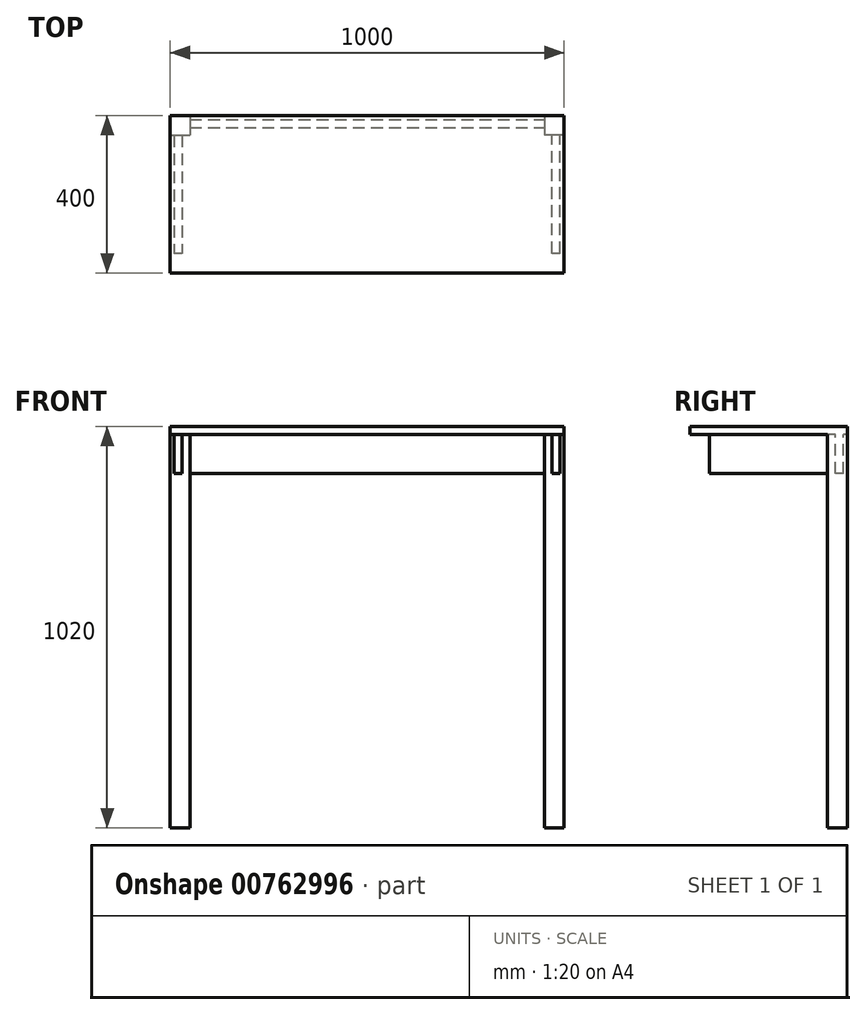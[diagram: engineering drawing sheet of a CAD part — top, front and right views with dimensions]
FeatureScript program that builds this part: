
annotation { "Feature Type Name" : "Feature", "Feature Type Description" : "" }
export const myFeature = defineFeature(function(context is Context, id is Id, definition is map)
    precondition{}
    {
        {
            var Q0;
            Q0=qCreatedBy(makeId("Top.planeOp"),FACE);
            var sketch = newSketch(context, id + "F0", { "sketchPlane" : qUnion([Q0])});
            skLineSegment(sketch, "E0.bottom", {"start": v(0, 0) * mm, "end": v(-1000, 0) * mm});
            skLineSegment(sketch, "E0.top", {"start": v(0, -400) * mm, "end": v(-1000, -400) * mm});
            skLineSegment(sketch, "E0.left", {"start": v(0, 0) * mm, "end": v(0, -400) * mm});
            skLineSegment(sketch, "E0.right", {"start": v(-1000, 0) * mm, "end": v(-1000, -400) * mm});
            skSolve(sketch);
        }
        {
            var Q0;
            Q0=makeQuery(id+"F0.imprint","IMPRINT",FACE,{"disambiguationData":[TD([[makeQuery(id+"F0.imprint","IMPRINT",EDGE,{"derivedFrom":sQuery(id+"F0.wireOp",EDGE,"E0.bottom")}),1.0]])]});
            extrude(context, id + "F1", {"entities" : qUnion([Q0]), "oppositeDirection" : true, "depth" : 20 * mm, "offsetDistance" : 25 * mm});
        }
        {
            var Q0;
            Q0=makeQuery(id+"F1.opExtrude","CAP_FACE",FACE,{"disambiguationData":[OSD([sQuery(id+"F0.wireOp",EDGE,"E0.bottom"),sQuery(id+"F0.wireOp",EDGE,"E0.top"),sQuery(id+"F0.wireOp",EDGE,"E0.left"),sQuery(id+"F0.wireOp",EDGE,"E0.right")])],"isStart":false});
            var sketch = newSketch(context, id + "F2", { "sketchPlane" : qUnion([Q0])});
            skLineSegment(sketch, "E1.bottom", {"start": v(0, 0) * mm, "end": v(-50, 0) * mm});
            skLineSegment(sketch, "E1.top", {"start": v(0, 50) * mm, "end": v(-50, 50) * mm});
            skLineSegment(sketch, "E1.left", {"start": v(0, 0) * mm, "end": v(0, 50) * mm});
            skLineSegment(sketch, "E1.right", {"start": v(-50, 0) * mm, "end": v(-50, 50) * mm});
            skLineSegment(sketch, "E2.bottom", {"start": v(-1000, 0) * mm, "end": v(-950, 0) * mm});
            skLineSegment(sketch, "E2.top", {"start": v(-1000, 50) * mm, "end": v(-950, 50) * mm});
            skLineSegment(sketch, "E2.left", {"start": v(-1000, 0) * mm, "end": v(-1000, 50) * mm});
            skLineSegment(sketch, "E2.right", {"start": v(-950, 0) * mm, "end": v(-950, 50) * mm});
            skSolve(sketch);
        }
        {
            var Q0;
            Q0 = qSketchRegion(id + "F2", true);
            extrude(context, id + "F3", {"entities" : qUnion([Q0]), "operationType" : NewBodyOperationType.ADD, "depth" : 1000 * mm, "offsetDistance" : 25 * mm});
        }
        {
            var Q0;
            Q0=makeQuery(id+"F1.opExtrude","CAP_FACE",FACE,{"disambiguationData":[OSD([sQuery(id+"F0.wireOp",EDGE,"E0.bottom"),sQuery(id+"F0.wireOp",EDGE,"E0.top"),sQuery(id+"F0.wireOp",EDGE,"E0.left"),sQuery(id+"F0.wireOp",EDGE,"E0.right")])],"isStart":false});
            var sketch = newSketch(context, id + "F4", { "sketchPlane" : qUnion([Q0])});
            skLineSegment(sketch, "E3.bottom", {"start": v(-950, 10) * mm, "end": v(-50, 10) * mm});
            skLineSegment(sketch, "E3.top", {"start": v(-950, 30) * mm, "end": v(-50, 30) * mm});
            skLineSegment(sketch, "E3.left", {"start": v(-950, 10) * mm, "end": v(-950, 30) * mm});
            skLineSegment(sketch, "E3.right", {"start": v(-50, 10) * mm, "end": v(-50, 30) * mm});
            skLineSegment(sketch, "E4.bottom", {"start": v(-10, 350) * mm, "end": v(-30, 350) * mm});
            skLineSegment(sketch, "E4.top", {"start": v(-10, 50) * mm, "end": v(-30, 50) * mm});
            skLineSegment(sketch, "E4.left", {"start": v(-10, 350) * mm, "end": v(-10, 50) * mm});
            skLineSegment(sketch, "E4.right", {"start": v(-30, 350) * mm, "end": v(-30, 50) * mm});
            skLineSegment(sketch, "E5.bottom", {"start": v(-970, 50) * mm, "end": v(-990, 50) * mm});
            skLineSegment(sketch, "E5.top", {"start": v(-970, 350) * mm, "end": v(-990, 350) * mm});
            skLineSegment(sketch, "E5.left", {"start": v(-970, 50) * mm, "end": v(-970, 350) * mm});
            skLineSegment(sketch, "E5.right", {"start": v(-990, 50) * mm, "end": v(-990, 350) * mm});
            skSolve(sketch);
        }
        {
            var Q0;
            Q0 = qSketchRegion(id + "F4", true);
            extrude(context, id + "F5", {"entities" : qUnion([Q0]), "operationType" : NewBodyOperationType.ADD, "depth" : 100 * mm, "offsetDistance" : 25 * mm});
        }
    });
